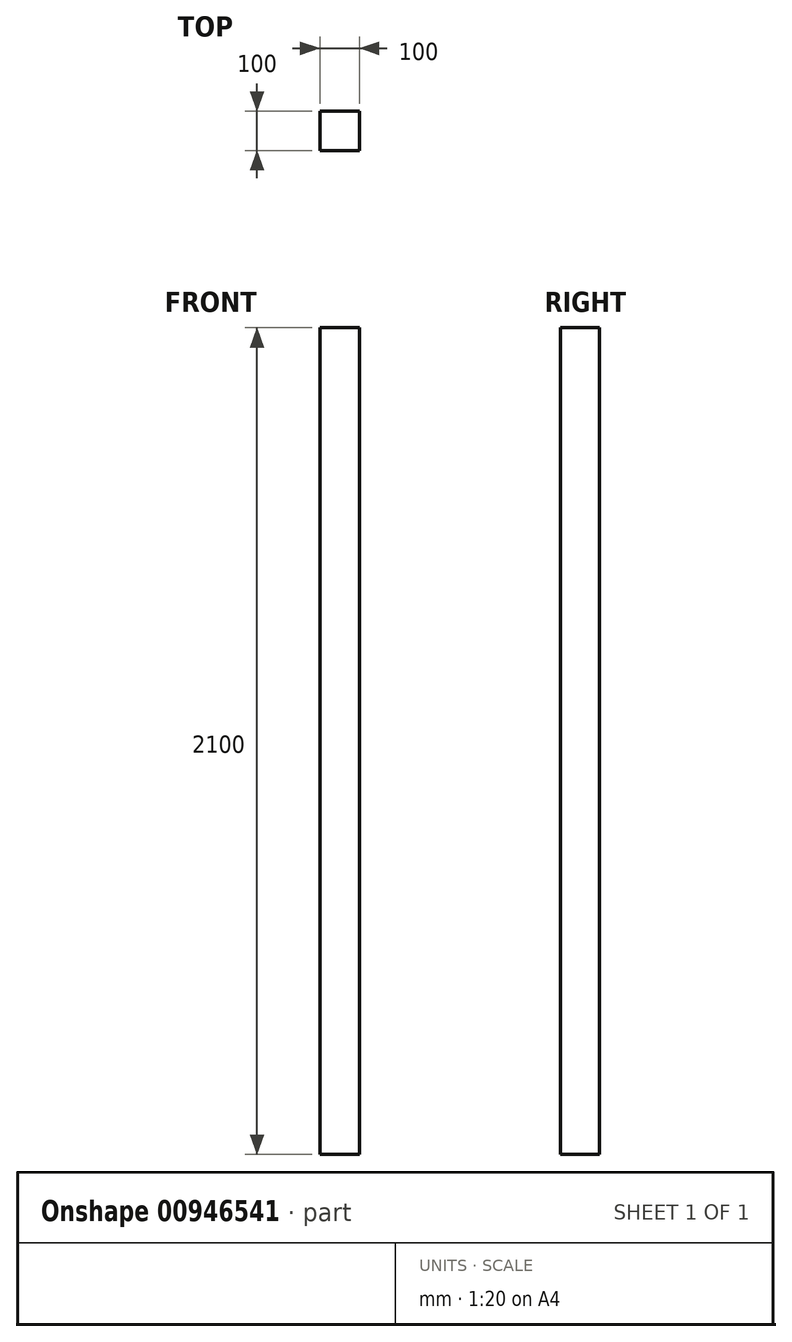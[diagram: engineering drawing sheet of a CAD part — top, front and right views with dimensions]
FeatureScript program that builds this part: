
annotation { "Feature Type Name" : "Feature", "Feature Type Description" : "" }
export const myFeature = defineFeature(function(context is Context, id is Id, definition is map)
    precondition{}
    {
        {
            var Q0;
            Q0=qCreatedBy(makeId("Top.planeOp"),FACE);
            var sketch = newSketch(context, id + "F0", { "sketchPlane" : qUnion([Q0])});
            skLineSegment(sketch, "E0.bottom", {"start": v(50, -50) * mm, "end": v(-50, -50) * mm});
            skLineSegment(sketch, "E0.top", {"start": v(50, 50) * mm, "end": v(-50, 50) * mm});
            skLineSegment(sketch, "E0.left", {"start": v(50, -50) * mm, "end": v(50, 50) * mm});
            skLineSegment(sketch, "E0.right", {"start": v(-50, -50) * mm, "end": v(-50, 50) * mm});
            skPoint(sketch, "E0.middle", {"position": v(0, 0) * mm});
            skSolve(sketch);
        }
        {
            var Q0;
            Q0=qSketchRegion(id+"F0",true);
            extrude(context, id + "F1", {"entities" : qUnion([Q0]), "depth" : 2100 * mm, "offsetDistance" : 25 * mm});
        }
    });
